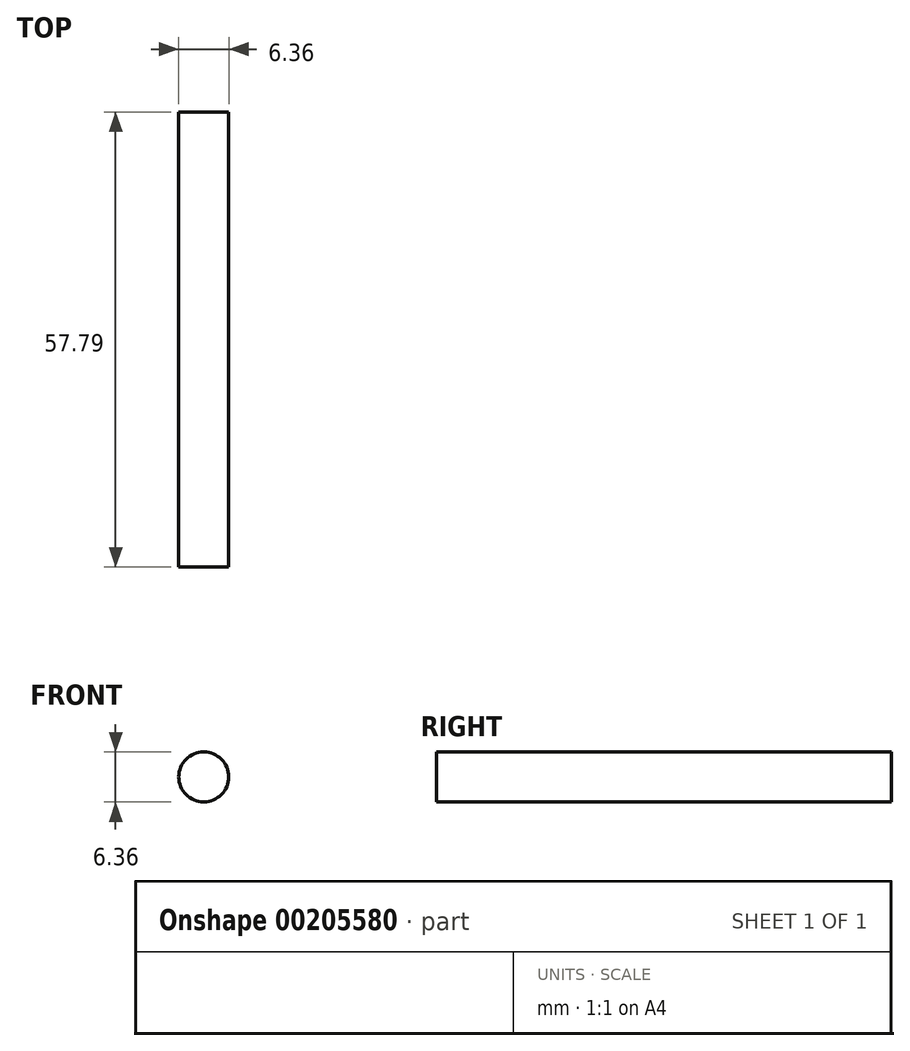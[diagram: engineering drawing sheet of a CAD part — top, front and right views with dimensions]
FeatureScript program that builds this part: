
annotation { "Feature Type Name" : "Feature", "Feature Type Description" : "" }
export const myFeature = defineFeature(function(context is Context, id is Id, definition is map)
    precondition{}
    {
        {
            var Q0;
            Q0=qCreatedBy(makeId("Front.planeOp"),FACE);
            var sketch = newSketch(context, id + "F0", { "sketchPlane" : qUnion([Q0])});
            skCircle(sketch, "E0", {"center": v(0, 0) * mm, "radius": 3.18 * mm});
            skSolve(sketch);
        }
        {
            var Q0;
            Q0=qSketchRegion(id+"F0",true);
            extrude(context, id + "F1", {"entities" : qUnion([Q0]), "flatOperationType" : FlatOperationType.REMOVE, "offsetDistance" : 25.4 * mm, "depth" : 57.78 * mm, "domain" : OperationDomain.MODEL});
        }
    });
